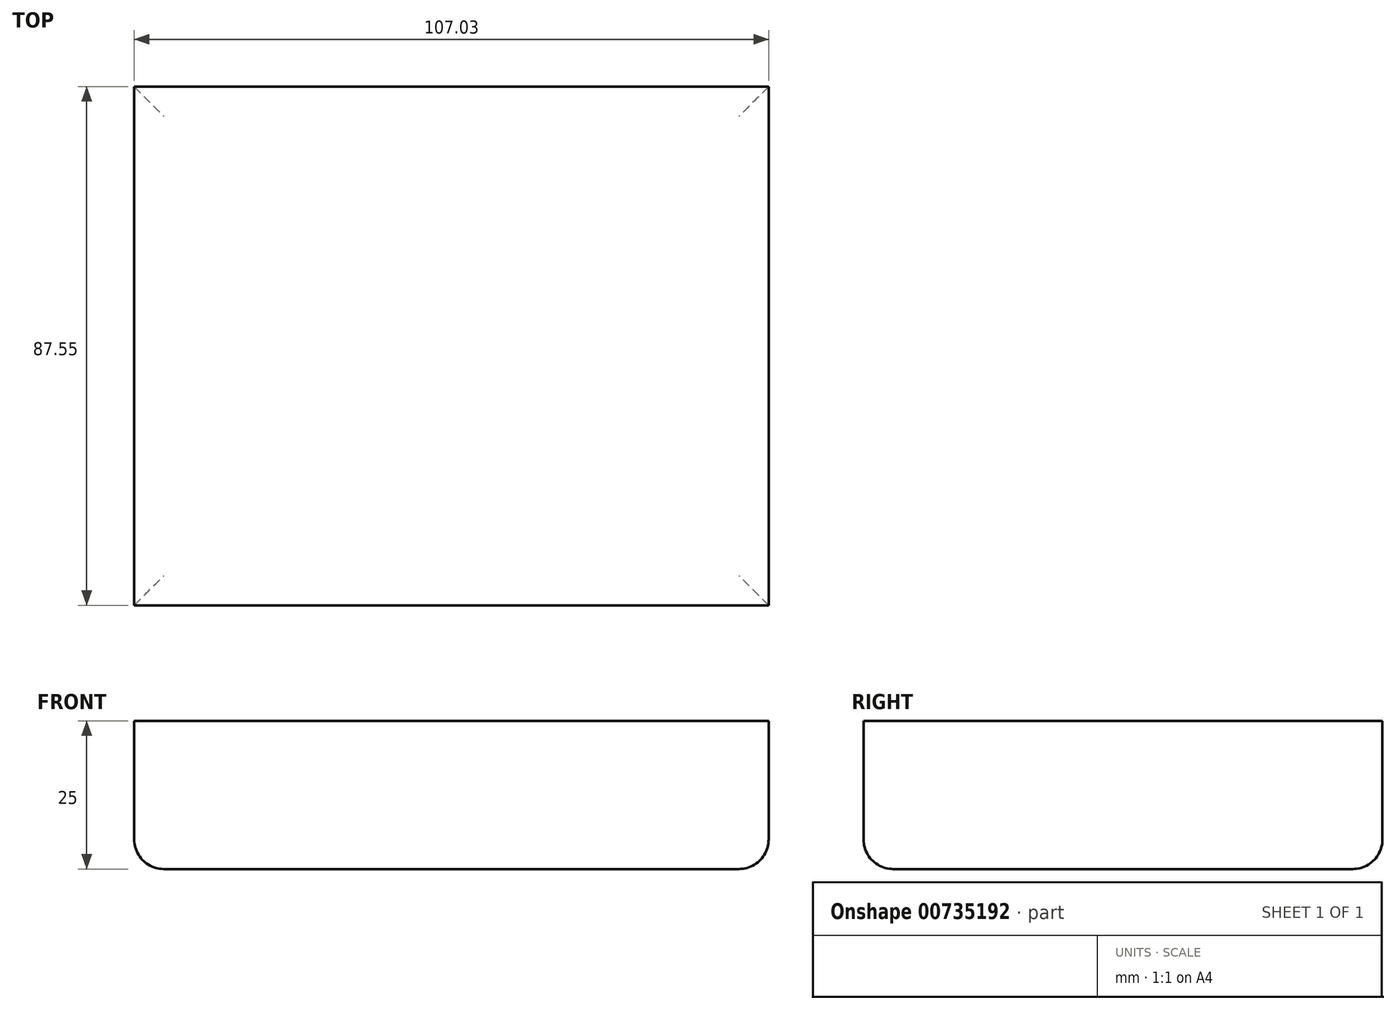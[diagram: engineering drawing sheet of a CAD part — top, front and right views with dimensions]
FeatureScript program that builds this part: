
annotation { "Feature Type Name" : "Feature", "Feature Type Description" : "" }
export const myFeature = defineFeature(function(context is Context, id is Id, definition is map)
    precondition{}
    {
        {
            var Q0;
            Q0=qCreatedBy(makeId("Top.planeOp"),FACE);
            var sketch = newSketch(context, id + "F0", { "sketchPlane" : qUnion([Q0])});
            skLineSegment(sketch, "E0", {"start": v(-57.84, 39.27) * mm, "end": v(49.19, 39.27) * mm});
            skLineSegment(sketch, "E1", {"start": v(49.19, 39.27) * mm, "end": v(49.19, -48.28) * mm});
            skLineSegment(sketch, "E2", {"start": v(49.19, -48.28) * mm, "end": v(-57.84, -48.28) * mm});
            skLineSegment(sketch, "E3", {"start": v(-57.84, -48.28) * mm, "end": v(-57.84, 39.27) * mm});
            skSolve(sketch);
        }
        {
            var Q0;
            Q0 = qSketchRegion(id + "F0", true);
            extrude(context, id + "F1", {"entities" : qUnion([Q0]), "depth" : 25 * mm, "offsetDistance" : 25 * mm});
        }
        {
            var Q0;
            Q0=makeQuery(id+"F1.opExtrude","CAP_EDGE",EDGE,{"disambiguationData":[OSD([sQuery(id+"F0.wireOp",EDGE,"E3")])],"isStart":true});
            var Q1;
            Q1=makeQuery(id+"F1.opExtrude","CAP_EDGE",EDGE,{"disambiguationData":[OSD([sQuery(id+"F0.wireOp",EDGE,"E0")])],"isStart":true});
            var Q2;
            Q2=makeQuery(id+"F1.opExtrude","CAP_EDGE",EDGE,{"disambiguationData":[OSD([sQuery(id+"F0.wireOp",EDGE,"E1")])],"isStart":true});
            var Q3;
            Q3=makeQuery(id+"F1.opExtrude","CAP_EDGE",EDGE,{"disambiguationData":[OSD([sQuery(id+"F0.wireOp",EDGE,"E2")])],"isStart":true});
            fillet(context, id + "F2", {"entities" : qUnion([Q0, Q1, Q2, Q3]), "radius" : 5 * mm, "tangentPropagation" : true, "allowEdgeOverflow" : false});
        }
    });
